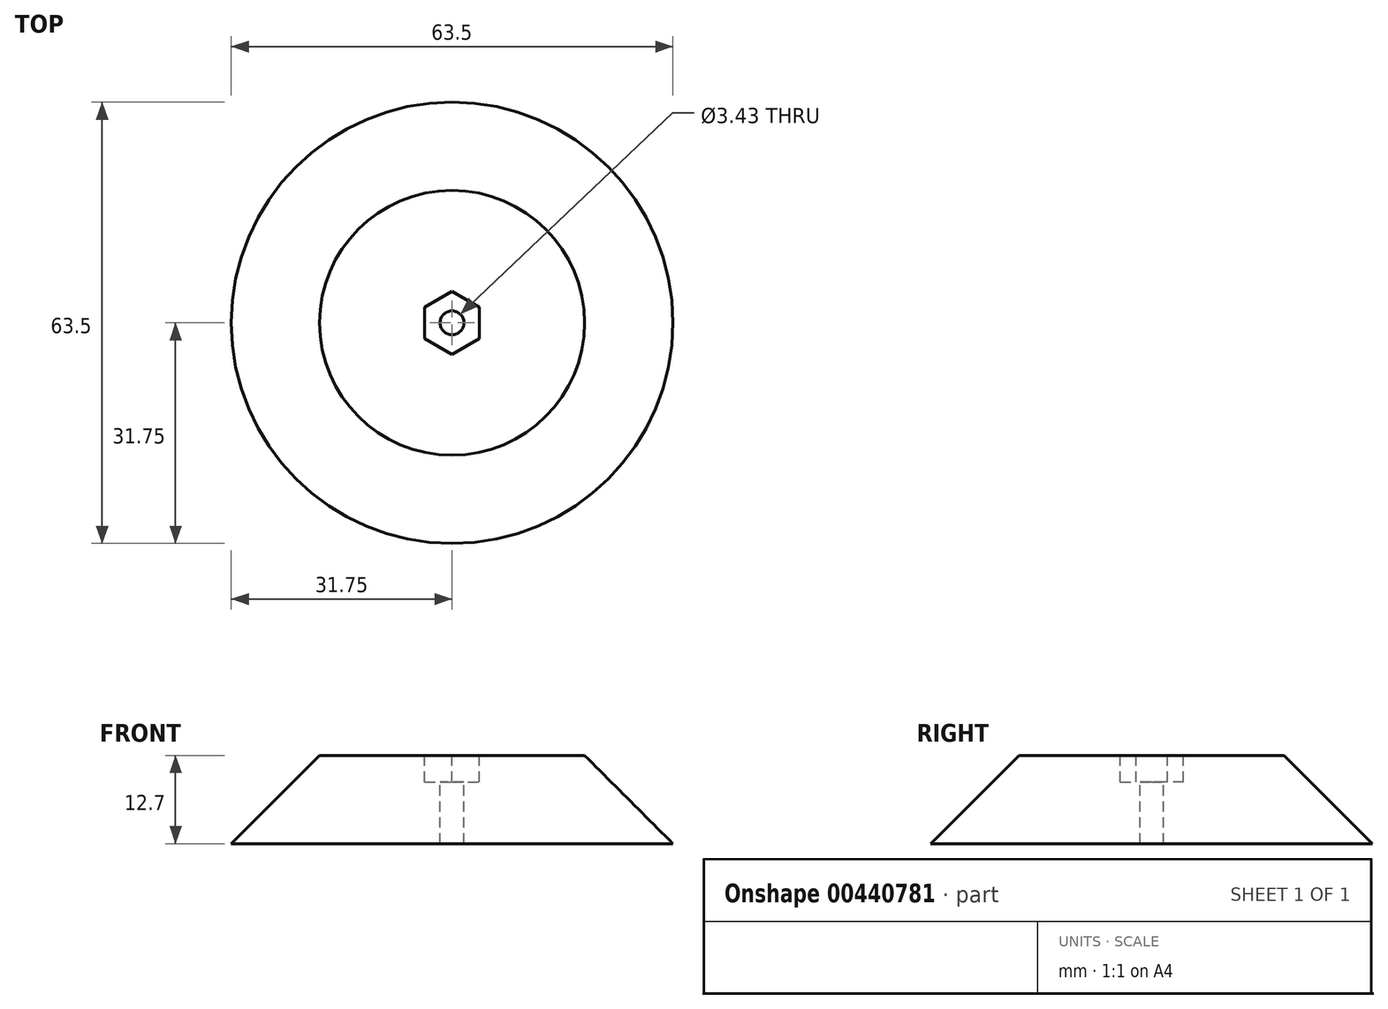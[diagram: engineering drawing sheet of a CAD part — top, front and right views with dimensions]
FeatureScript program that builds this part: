
annotation { "Feature Type Name" : "Feature", "Feature Type Description" : "" }
export const myFeature = defineFeature(function(context is Context, id is Id, definition is map)
    precondition{}
    {
        {
            var Q0;
            Q0=qCreatedBy(makeId("Top.planeOp"),FACE);
            var sketch = newSketch(context, id + "F0", { "sketchPlane" : qUnion([Q0])});
            skCircle(sketch, "E0", {"center": v(-31.75, 31.75) * mm, "radius": 31.75 * mm});
            skCircle(sketch, "E1", {"center": v(-31.75, 31.75) * mm, "radius": 1.71 * mm});
            skSolve(sketch);
        }
        {
            var Q0;
            Q0=qCreatedBy(makeId("Top.planeOp"),FACE);
            cPlane(context, id + "F1", {"entities" : qUnion([Q0]), "cplaneType" : CPlaneType.OFFSET, "offset" : 12.7 * mm, "width" : 152.4 * mm, "height" : 152.4 * mm});
        }
        {
            var Q0;
            Q0=qCreatedBy(id+"F1.planeOp",FACE);
            var sketch = newSketch(context, id + "F2", { "sketchPlane" : qUnion([Q0])});
            skCircle(sketch, "E2", {"center": v(-31.75, 31.75) * mm, "radius": 1.71 * mm});
            skCircle(sketch, "E3", {"center": v(-31.75, 31.75) * mm, "radius": 25.4 * mm});
            skSolve(sketch);
        }
        {
            var Q0;
            Q0=qCreatedBy(makeId("Front.planeOp"),FACE);
            var Q1;
            Q1=sQuery(id+"F2.wireOp",VERTEX,"E2.center");
            cPlane(context, id + "F3", {"entities" : qUnion([Q0, Q1]), "cplaneType" : CPlaneType.PLANE_POINT, "offset" : 25.4 * mm, "width" : 152.4 * mm, "height" : 152.4 * mm});
        }
        {
            var Q0;
            Q0=makeQuery(id+"F2.imprint","IMPRINT",FACE,{"disambiguationData":[TD([[makeQuery(id+"F2.imprint","IMPRINT",EDGE,{"derivedFrom":sQuery(id+"F2.wireOp",EDGE,"E2")}),-1.0]])]});
            extrude(context, id + "F4", {"entities" : qUnion([Q0]), "oppositeDirection" : true, "depth" : 12.7 * mm});
        }
        {
            var Q0;
            Q0=makeQuery(id+"F0.imprint","IMPRINT",FACE,{"disambiguationData":[TD([[makeQuery(id+"F0.imprint","IMPRINT",EDGE,{"derivedFrom":sQuery(id+"F0.wireOp",EDGE,"E0")}),1.0]])]});
            extrude(context, id + "F5", {"entities" : qUnion([Q0]), "operationType" : NewBodyOperationType.ADD, "depth" : 12.7 * mm});
        }
        {
            var Q0;
            Q0=makeQuery(id+"F5.boolean.opBoolean","MERGE",FACE,{"derivedFrom":[makeQuery(id+"F4.opExtrude","CAP_FACE",FACE,{"disambiguationData":[OSD([sQuery(id+"F2.wireOp",EDGE,"E2"),sQuery(id+"F2.wireOp",EDGE,"E3")])],"isStart":true}),makeQuery(id+"F5.opExtrude","CAP_FACE",FACE,{"disambiguationData":[OSD([sQuery(id+"F0.wireOp",EDGE,"E0"),sQuery(id+"F0.wireOp",EDGE,"E1")])],"isStart":false})]});
            var sketch = newSketch(context, id + "F6", { "sketchPlane" : qUnion([Q0])});
            skCircle(sketch, "E4.cCircle", {"center": v(-31.75, 31.75) * mm, "radius": 3.94 * mm, "construction": true});
            skLineSegment(sketch, "E4.0", {"start": v(-27.81, 34.02) * mm, "end": v(-27.81, 29.48) * mm});
            skLineSegment(sketch, "E4.1", {"start": v(-27.81, 29.48) * mm, "end": v(-31.75, 27.2) * mm});
            skLineSegment(sketch, "E4.2", {"start": v(-31.75, 27.2) * mm, "end": v(-35.69, 29.48) * mm});
            skLineSegment(sketch, "E4.3", {"start": v(-35.69, 29.48) * mm, "end": v(-35.69, 34.02) * mm});
            skLineSegment(sketch, "E4.4", {"start": v(-35.69, 34.02) * mm, "end": v(-31.75, 36.3) * mm});
            skLineSegment(sketch, "E4.5", {"start": v(-31.75, 36.3) * mm, "end": v(-27.81, 34.02) * mm});
            skPoint(sketch, "E4.0.midPoint", {"position": v(-27.81, 31.75) * mm});
            skSolve(sketch);
        }
        {
            var Q0;
            Q0=makeQuery(id+"F6.imprint","IMPRINT",FACE,{"disambiguationData":[TD([[makeQuery(id+"F6.imprint","IMPRINT",EDGE,{"derivedFrom":sQuery(id+"F6.wireOp",EDGE,"E4.0")}),-1.0]])]});
            extrude(context, id + "F7", {"entities" : qUnion([Q0]), "operationType" : NewBodyOperationType.REMOVE, "oppositeDirection" : true, "depth" : 3.8 * mm});
        }
        {
            var Q0;
            Q0=makeQuery(id+"F5.opExtrude","CAP_EDGE",EDGE,{"disambiguationData":[OSD([sQuery(id+"F0.wireOp",EDGE,"E0")])],"isStart":false});
            chamfer(context, id + "F8", {"entities" : qUnion([Q0]), "chamferType" : ChamferType.OFFSET_ANGLE, "width" : 12.7 * mm, "oppositeDirection" : false, "angle" : 45 * degree, "tangentPropagation" : true});
        }
    });
